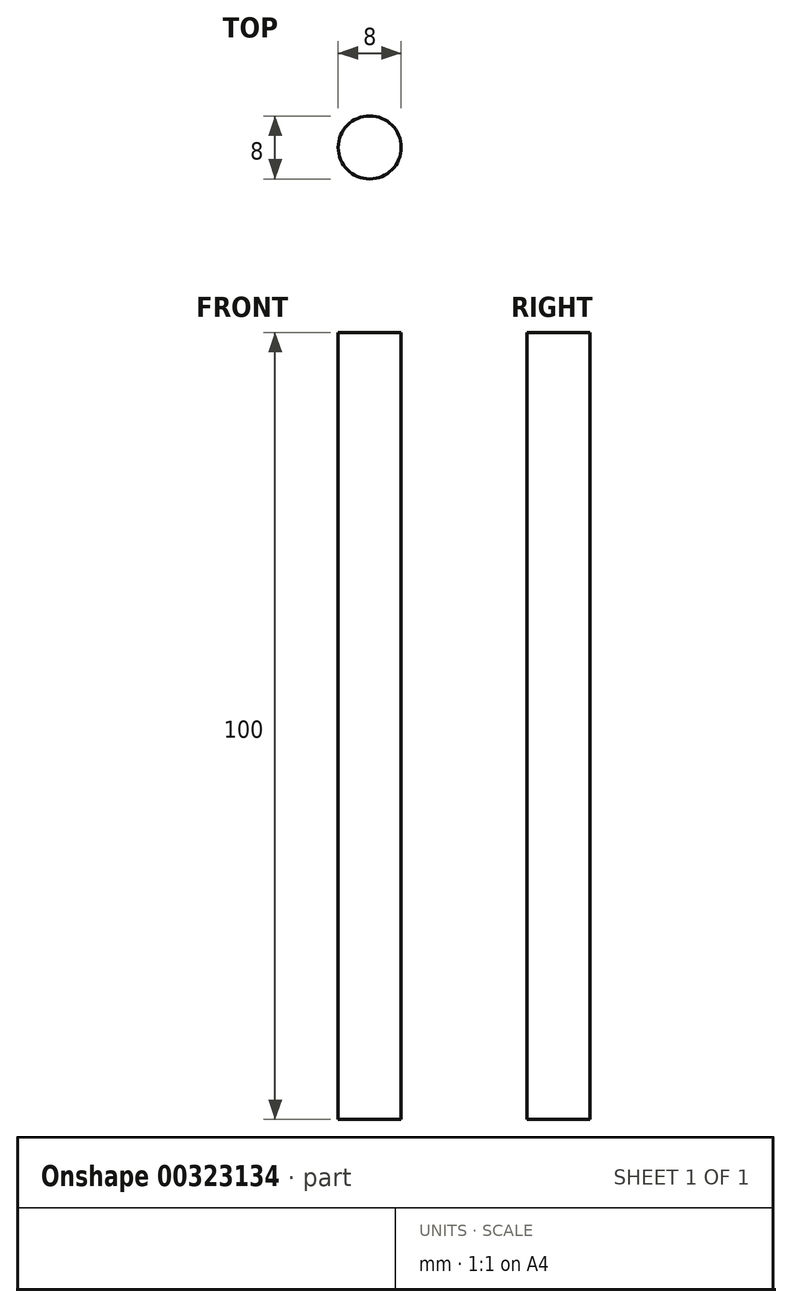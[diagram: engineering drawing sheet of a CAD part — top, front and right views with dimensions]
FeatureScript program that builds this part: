
annotation { "Feature Type Name" : "Feature", "Feature Type Description" : "" }
export const myFeature = defineFeature(function(context is Context, id is Id, definition is map)
    precondition{}
    {
        {
            var Q0;
            Q0=qCreatedBy(makeId("Top.planeOp"),FACE);
            var sketch = newSketch(context, id + "F0", { "sketchPlane" : qUnion([Q0])});
            skCircle(sketch, "E0", {"center": v(0, 0) * mm, "radius": 4 * mm});
            skSolve(sketch);
        }
        {
            var Q0;
            Q0=makeQuery(id+"F0.imprint","IMPRINT",FACE,{"disambiguationData":[TD([[makeQuery(id+"F0.imprint","IMPRINT",EDGE,{"derivedFrom":sQuery(id+"F0.wireOp",EDGE,"E0")}),1.0]])]});
            extrude(context, id + "F1", {"entities" : qUnion([Q0]), "depth" : 100 * mm});
        }
    });
